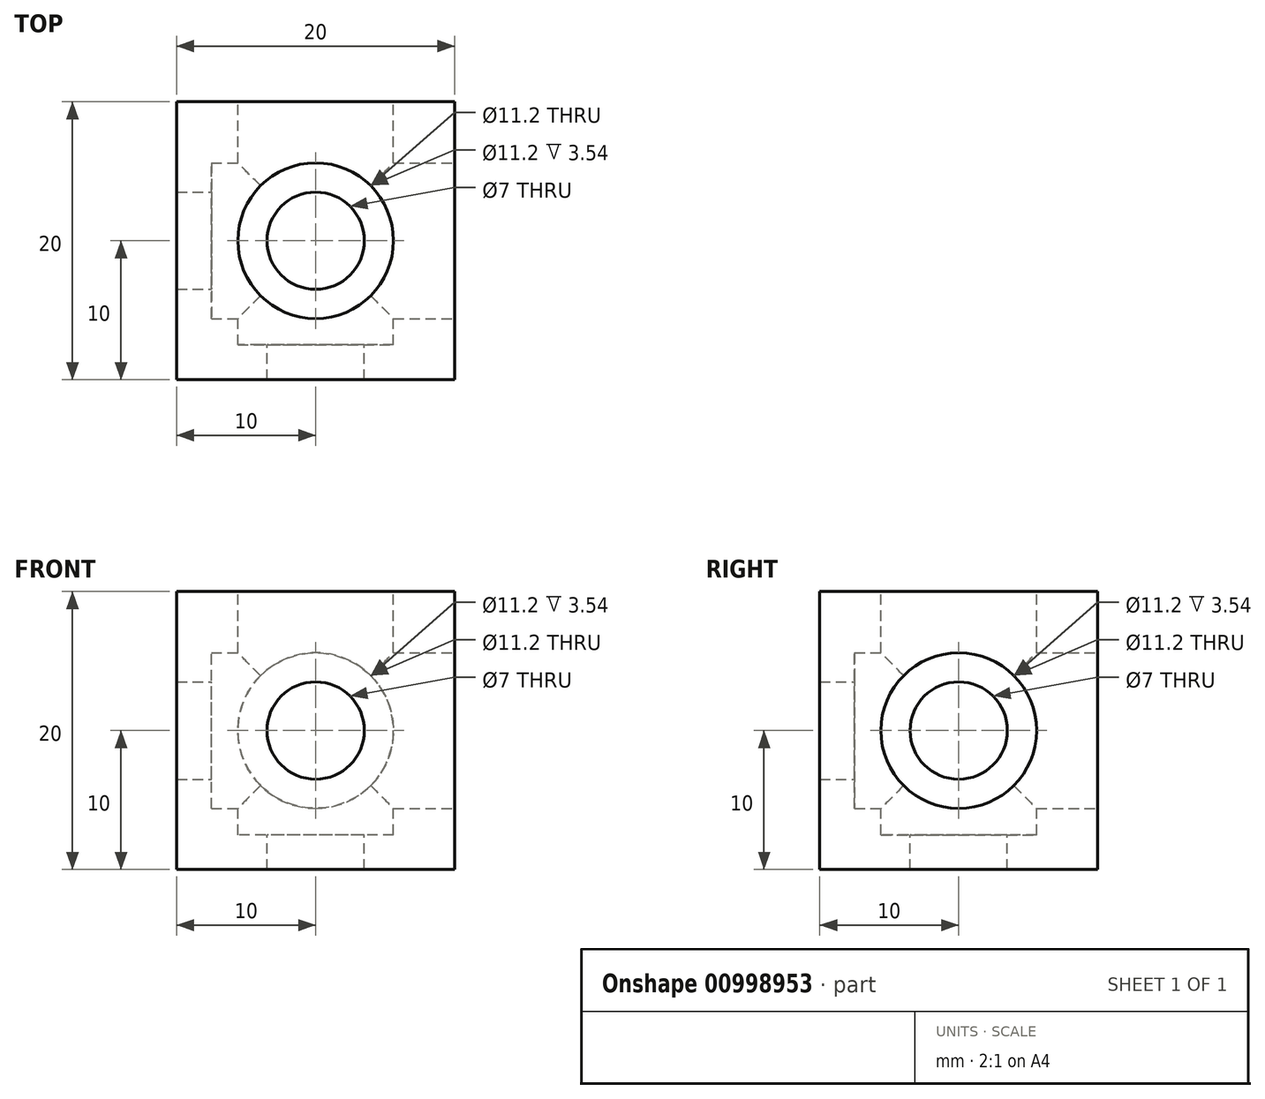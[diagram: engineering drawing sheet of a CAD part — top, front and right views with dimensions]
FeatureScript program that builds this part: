
annotation { "Feature Type Name" : "Feature", "Feature Type Description" : "" }
export const myFeature = defineFeature(function(context is Context, id is Id, definition is map)
    precondition{}
    {
        {
            var Q0;
            Q0=qCreatedBy(makeId("Front.planeOp"),FACE);
            var sketch = newSketch(context, id + "F0", { "sketchPlane" : qUnion([Q0])});
            skLineSegment(sketch, "E0.bottom", {"start": v(10, 10) * mm, "end": v(-10, 10) * mm});
            skLineSegment(sketch, "E0.top", {"start": v(10, -10) * mm, "end": v(-10, -10) * mm});
            skLineSegment(sketch, "E0.left", {"start": v(10, 10) * mm, "end": v(10, -10) * mm});
            skLineSegment(sketch, "E0.right", {"start": v(-10, 10) * mm, "end": v(-10, -10) * mm});
            skPoint(sketch, "E0.middle", {"position": v(0, 0) * mm});
            skCircle(sketch, "E1", {"center": v(0, 0) * mm, "radius": 3.5 * mm});
            skCircle(sketch, "E2", {"center": v(0, 0) * mm, "radius": 5.6 * mm});
            skSolve(sketch);
        }
        {
            var Q0;
            Q0=makeQuery(id+"F0.imprint","IMPRINT",FACE,{"disambiguationData":[TD([[makeQuery(id+"F0.imprint","IMPRINT",EDGE,{"derivedFrom":sQuery(id+"F0.wireOp",EDGE,"E0.bottom")}),1.0]])]});
            extrude(context, id + "F1", {"entities" : qUnion([Q0]), "depth" : 20 * mm, "offsetDistance" : 25 * mm});
        }
        {
            var Q0;
            Q0=makeQuery(id+"F0.imprint","IMPRINT",FACE,{"disambiguationData":[TD([[makeQuery(id+"F0.imprint","IMPRINT",EDGE,{"derivedFrom":sQuery(id+"F0.wireOp",EDGE,"E1")}),-1.0]])]});
            extrude(context, id + "F2", {"entities" : qUnion([Q0]), "operationType" : NewBodyOperationType.ADD, "depth" : 20 * mm, "offsetDistance" : 25 * mm, "hasSecondDirection" : true, "secondDirectionOppositeDirection" : false, "secondDirectionDepth" : 17.5 * mm});
        }
        {
            var Q0;
            Q0=makeQuery(id+"F1.opExtrude","SWEPT_FACE",FACE,{"disambiguationData":[OSD([sQuery(id+"F0.wireOp",EDGE,"E0.left")])]});
            var sketch = newSketch(context, id + "F3", { "sketchPlane" : qUnion([Q0])});
            skLineSegment(sketch, "E3", {"start": v(-20, 10) * mm, "end": v(0, -10) * mm, "construction": true});
            skCircle(sketch, "E4", {"center": v(-10, 0) * mm, "radius": 3.5 * mm});
            skCircle(sketch, "E5", {"center": v(-10, 0) * mm, "radius": 5.6 * mm});
            skSolve(sketch);
        }
        {
            var Q0;
            Q0=makeQuery(id+"F3.imprint","IMPRINT",FACE,{"disambiguationData":[TD([[makeQuery(id+"F3.imprint","IMPRINT",EDGE,{"derivedFrom":sQuery(id+"F3.wireOp",EDGE,"E4")}),-1.0]])]});
            var Q1;
            Q1=makeQuery(id+"F3.imprint","IMPRINT",FACE,{"disambiguationData":[TD([[makeQuery(id+"F3.imprint","IMPRINT",EDGE,{"derivedFrom":sQuery(id+"F3.wireOp",EDGE,"E4")}),1.0]])]});
            extrude(context, id + "F4", {"entities" : qUnion([Q0, Q1]), "operationType" : NewBodyOperationType.REMOVE, "oppositeDirection" : true, "depth" : 25 * mm, "offsetDistance" : 25 * mm});
        }
        {
            var Q0;
            Q0=makeQuery(id+"F3.imprint","IMPRINT",FACE,{"disambiguationData":[TD([[makeQuery(id+"F3.imprint","IMPRINT",EDGE,{"derivedFrom":sQuery(id+"F3.wireOp",EDGE,"E4")}),-1.0]])]});
            extrude(context, id + "F5", {"entities" : qUnion([Q0]), "operationType" : NewBodyOperationType.ADD, "oppositeDirection" : true, "depth" : 20 * mm, "offsetDistance" : 25 * mm, "hasSecondDirection" : true, "secondDirectionOppositeDirection" : true, "secondDirectionDepth" : 17.5 * mm});
        }
        {
            var Q0;
            Q0=makeQuery(id+"F1.opExtrude","SWEPT_FACE",FACE,{"disambiguationData":[OSD([sQuery(id+"F0.wireOp",EDGE,"E0.bottom")])]});
            var sketch = newSketch(context, id + "F6", { "sketchPlane" : qUnion([Q0])});
            skLineSegment(sketch, "E6", {"start": v(-10, -20) * mm, "end": v(10, 0) * mm, "construction": true});
            skCircle(sketch, "E7", {"center": v(0, -10) * mm, "radius": 5.6 * mm});
            skCircle(sketch, "E8", {"center": v(0, -10) * mm, "radius": 3.5 * mm});
            skSolve(sketch);
        }
        {
            var Q0;
            Q0=makeQuery(id+"F6.imprint","IMPRINT",FACE,{"disambiguationData":[TD([[makeQuery(id+"F6.imprint","IMPRINT",EDGE,{"derivedFrom":sQuery(id+"F6.wireOp",EDGE,"E7")}),1.0]])]});
            var Q1;
            Q1=makeQuery(id+"F6.imprint","IMPRINT",FACE,{"disambiguationData":[TD([[makeQuery(id+"F6.imprint","IMPRINT",EDGE,{"derivedFrom":sQuery(id+"F6.wireOp",EDGE,"E8")}),1.0]])]});
            extrude(context, id + "F7", {"entities" : qUnion([Q0, Q1]), "operationType" : NewBodyOperationType.REMOVE, "oppositeDirection" : true, "depth" : 25 * mm, "offsetDistance" : 25 * mm});
        }
        {
            var Q0;
            Q0=makeQuery(id+"F6.imprint","IMPRINT",FACE,{"disambiguationData":[TD([[makeQuery(id+"F6.imprint","IMPRINT",EDGE,{"derivedFrom":sQuery(id+"F6.wireOp",EDGE,"E7")}),1.0]])]});
            extrude(context, id + "F8", {"entities" : qUnion([Q0]), "operationType" : NewBodyOperationType.ADD, "oppositeDirection" : true, "depth" : 20 * mm, "offsetDistance" : 25 * mm, "hasSecondDirection" : true, "secondDirectionOppositeDirection" : true, "secondDirectionDepth" : 17.5 * mm});
        }
    });
